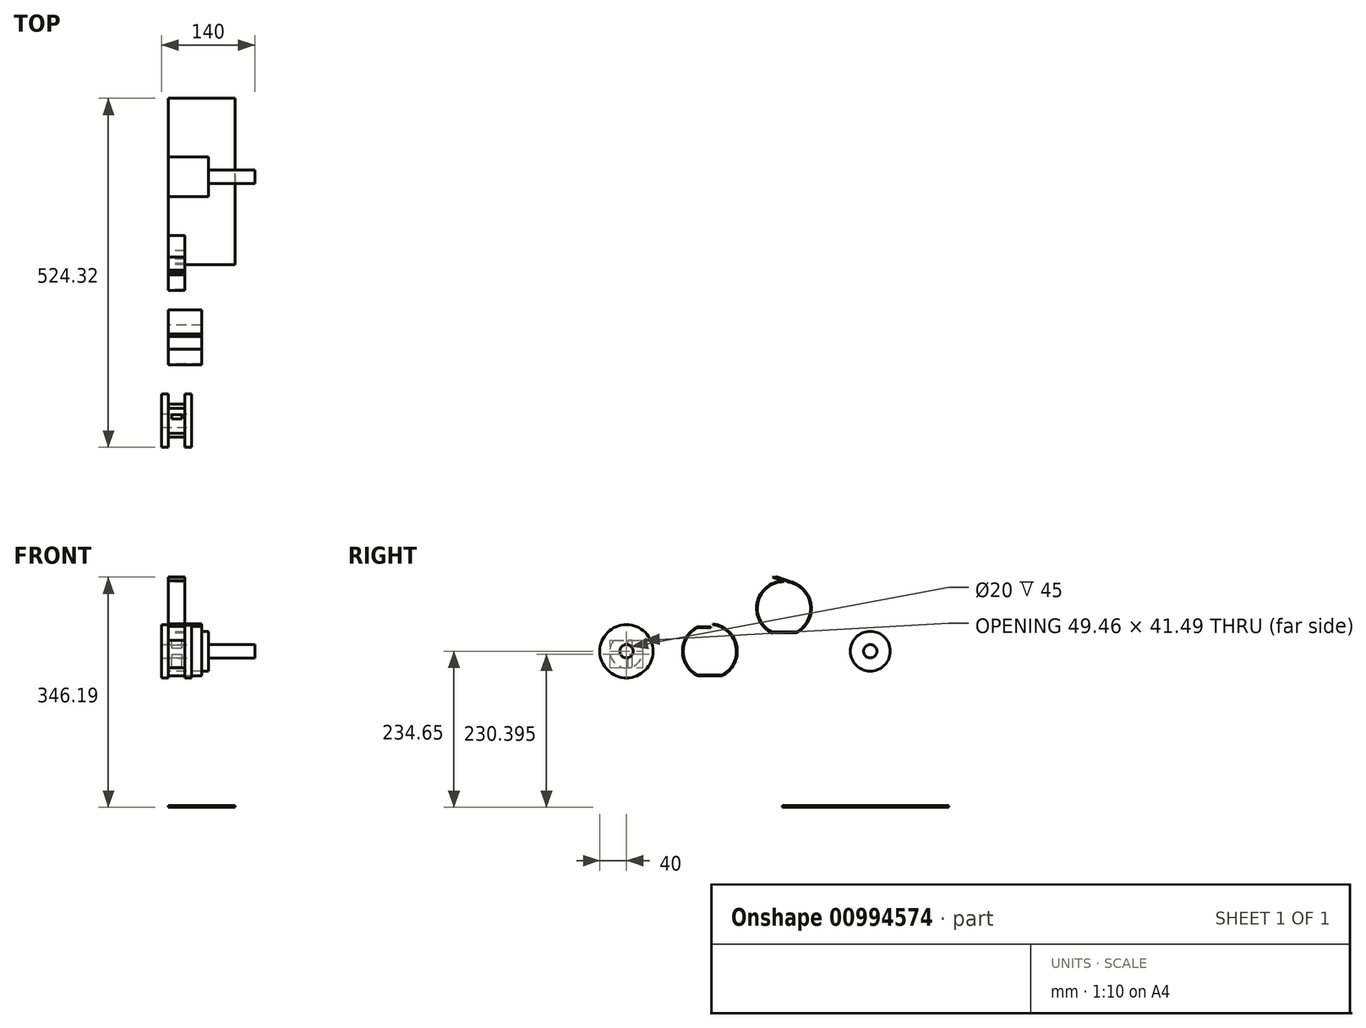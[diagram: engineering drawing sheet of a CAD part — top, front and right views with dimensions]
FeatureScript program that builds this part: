
annotation { "Feature Type Name" : "Feature", "Feature Type Description" : "" }
export const myFeature = defineFeature(function(context is Context, id is Id, definition is map)
    precondition{}
    {
        {
            var Q0;
            Q0=qCreatedBy(makeId("Right.planeOp"),FACE);
            var sketch = newSketch(context, id + "F0", { "sketchPlane" : qUnion([Q0])});
            skArc(sketch, "E0", {"start": v(-18.8, 16.49) * mm, "mid": v(0, -25) * mm, "end": v(18.8, 16.49) * mm});
            skLineSegment(sketch, "E1", {"start": v(-18.8, 16.49) * mm, "end": v(18.8, 16.49) * mm});
            skArc(sketch, "E2", {"start": v(106.71, 35.42) * mm, "mid": v(85.3, 0) * mm, "end": v(106.71, -35.42) * mm});
            skArc(sketch, "E3", {"start": v(107.38, 37.16) * mm, "mid": v(84.05, 0) * mm, "end": v(107.38, -37.16) * mm});
            skLineSegment(sketch, "E4", {"start": v(85.3, 0) * mm, "end": v(165.3, 0) * mm, "construction": true});
            skLineSegment(sketch, "E5", {"start": v(106.71, 35.42) * mm, "end": v(126.7, 35.42) * mm});
            skLineSegment(sketch, "E6", {"start": v(125.3, 37) * mm, "end": v(125.3, 41.25) * mm});
            skLineSegment(sketch, "E7", {"start": v(107.38, 37.16) * mm, "end": v(125.3, 37) * mm});
            skLineSegment(sketch, "E8.MirrorCS", {"start": v(106.71, -35.42) * mm, "end": v(143.9, -35.42) * mm});
            skLineSegment(sketch, "E9.MirrorCS", {"start": v(107.38, -37.16) * mm, "end": v(143.9, -36.82) * mm});
            skPoint(sketch, "E10.end.orphan", {"position": v(104.16, 35.42) * mm});
            skLineSegment(sketch, "E11", {"start": v(126.7, 39.98) * mm, "end": v(126.7, 35.42) * mm});
            skPoint(sketch, "E12.orphan", {"position": v(125.3, 35.42) * mm});
            skArc(sketch, "E13.trimOffspring", {"start": v(143.9, -35.42) * mm, "mid": v(164.3, 8.9) * mm, "end": v(126.7, 39.98) * mm});
            skArc(sketch, "E14.trimOffspring", {"start": v(143.9, -36.82) * mm, "mid": v(165.43, 9.55) * mm, "end": v(125.3, 41.25) * mm});
            skPoint(sketch, "E15.MirrorCS.end.orphan", {"position": v(104.16, -35.42) * mm});
            skPoint(sketch, "E15.MirrorCS.start.orphan", {"position": v(106.71, -35.42) * mm});
            skPoint(sketch, "E16.MirrorCS.end.orphan", {"position": v(146.45, -35.42) * mm});
            skCircle(sketch, "E17", {"center": v(366.34, 0) * mm, "radius": 30 * mm});
            skLineSegment(sketch, "E18", {"start": v(234.32, -232.15) * mm, "end": v(484.32, -232.15) * mm});
            skLineSegment(sketch, "E19", {"start": v(484.32, -232.15) * mm, "end": v(484.32, -234.65) * mm});
            skLineSegment(sketch, "E20", {"start": v(484.32, -234.65) * mm, "end": v(234.32, -234.65) * mm});
            skLineSegment(sketch, "E21", {"start": v(234.32, -234.65) * mm, "end": v(234.32, -232.15) * mm});
            skPoint(sketch, "E22.end.orphan", {"position": v(146.45, 35.42) * mm});
            skPoint(sketch, "E22.start.orphan", {"position": v(143.9, 35.42) * mm});
            skPoint(sketch, "E23.trimOffspring.end.orphan", {"position": v(143.9, 36.82) * mm});
            skLineSegment(sketch, "E24", {"start": v(112.79, 46.1) * mm, "end": v(112.75, 45.15) * mm});
            skArc(sketch, "E25", {"start": v(218.77, 101.6) * mm, "mid": v(195.43, 64.44) * mm, "end": v(218.77, 27.29) * mm});
            skLineSegment(sketch, "E26.MirrorCS", {"start": v(218.1, 29.03) * mm, "end": v(255.28, 29.03) * mm});
            skLineSegment(sketch, "E27.MirrorCS", {"start": v(218.77, 27.29) * mm, "end": v(255.28, 27.62) * mm});
            skPoint(sketch, "E28.end.orphan", {"position": v(215.54, 99.86) * mm});
            skPoint(sketch, "E29.orphan", {"position": v(236.68, 99.86) * mm});
            skArc(sketch, "E30.trimOffspring", {"start": v(255.28, 27.62) * mm, "mid": v(277.64, 69.33) * mm, "end": v(246.1, 104.6) * mm});
            skPoint(sketch, "E31.MirrorCS.end.orphan", {"position": v(215.54, 29.03) * mm});
            skPoint(sketch, "E31.MirrorCS.start.orphan", {"position": v(218.1, 29.03) * mm});
            skPoint(sketch, "E32.MirrorCS.end.orphan", {"position": v(257.83, 29.03) * mm});
            skPoint(sketch, "E33.end.orphan", {"position": v(257.83, 99.86) * mm});
            skPoint(sketch, "E33.start.orphan", {"position": v(255.28, 99.86) * mm});
            skPoint(sketch, "E34.trimOffspring.end.orphan", {"position": v(255.28, 101.27) * mm});
            skArc(sketch, "E35", {"start": v(234.63, 105.64) * mm, "mid": v(196.25, 72.63) * mm, "end": v(218.77, 27.29) * mm});
            skArc(sketch, "E36", {"start": v(255.28, 29.03) * mm, "mid": v(276.11, 71.2) * mm, "end": v(242.43, 104.03) * mm});
            skLineSegment(sketch, "E37", {"start": v(246.1, 104.6) * mm, "end": v(226.45, 111.54) * mm});
            skLineSegment(sketch, "E38", {"start": v(234.63, 105.64) * mm, "end": v(219.42, 111.1) * mm});
            skLineSegment(sketch, "E39", {"start": v(223.76, 111.4) * mm, "end": v(242.43, 104.82) * mm});
            skLineSegment(sketch, "E40", {"start": v(221.42, 111.4) * mm, "end": v(236.45, 106.1) * mm});
            skLineSegment(sketch, "E41", {"start": v(236.45, 106.1) * mm, "end": v(236.45, 104.44) * mm});
            skLineSegment(sketch, "E42", {"start": v(242.43, 104.82) * mm, "end": v(242.43, 104.03) * mm});
            skArc(sketch, "E43.trimOffspring", {"start": v(236.45, 104.44) * mm, "mid": v(197.82, 73.9) * mm, "end": v(218.1, 29.03) * mm});
            skPoint(sketch, "E44.start.orphan", {"position": v(215.71, 112.43) * mm});
            skPoint(sketch, "E45.orphan", {"position": v(223.92, 112.43) * mm});
            skLineSegment(sketch, "E46", {"start": v(223.76, 111.4) * mm, "end": v(226.45, 111.54) * mm});
            skLineSegment(sketch, "E47", {"start": v(221.42, 111.4) * mm, "end": v(219.42, 111.1) * mm});
            skPoint(sketch, "E48.end.orphan", {"position": v(218.22, 111.4) * mm});
            skPoint(sketch, "E49.end.orphan", {"position": v(236.45, 105.73) * mm});
            skSolve(sketch);
        }
        {
            var Q0;
            Q0=makeQuery(id+"F0.imprint","IMPRINT",FACE,{"disambiguationData":[TD([[makeQuery(id+"F0.imprint","IMPRINT",EDGE,{"derivedFrom":sQuery(id+"F0.wireOp",EDGE,"E0")}),1.0]])]});
            extrude(context, id + "F1", {"entities" : qUnion([Q0]), "depth" : 25 * mm, "offsetDistance" : 25 * mm});
        }
        {
            var Q0;
            Q0=makeQuery(id+"F1.opExtrude","CAP_FACE",FACE,{"disambiguationData":[OSD([sQuery(id+"F0.wireOp",EDGE,"E0"),sQuery(id+"F0.wireOp",EDGE,"E1")])],"isStart":false});
            var sketch = newSketch(context, id + "F2", { "sketchPlane" : qUnion([Q0])});
            skCircle(sketch, "E50", {"center": v(0, 0) * mm, "radius": 40 * mm});
            skSolve(sketch);
        }
        {
            var Q0;
            Q0=makeQuery(id+"F2.imprint","IMPRINT",FACE,{"disambiguationData":[TD([[makeQuery(id+"F2.imprint","IMPRINT",EDGE,{"derivedFrom":sQuery(id+"F2.wireOp",EDGE,"E50")}),1.0]])]});
            var Q1;
            Q1=makeQuery(id+"F2.imprint","IMPRINT",FACE,{"disambiguationData":[TD([[makeQuery(id+"F2.imprint","IMPRINT",EDGE,{"derivedFrom":makeQuery(id+"F1.opExtrude","CAP_EDGE",EDGE,{"disambiguationData":[OSD([sQuery(id+"F0.wireOp",EDGE,"E0")])],"isStart":false})}),1.0]])]});
            extrude(context, id + "F3", {"entities" : qUnion([Q0, Q1]), "operationType" : NewBodyOperationType.ADD, "depth" : 10 * mm, "offsetDistance" : 25 * mm});
        }
        {
            var Q0;
            Q0=makeQuery(id+"F1.opExtrude","CAP_FACE",FACE,{"disambiguationData":[OSD([sQuery(id+"F0.wireOp",EDGE,"E0"),sQuery(id+"F0.wireOp",EDGE,"E1")])],"isStart":true});
            var sketch = newSketch(context, id + "F4", { "sketchPlane" : qUnion([Q0])});
            skCircle(sketch, "E51", {"center": v(0, 0) * mm, "radius": 40 * mm});
            skSolve(sketch);
        }
        {
            var Q0;
            Q0=makeQuery(id+"F4.imprint","IMPRINT",FACE,{"disambiguationData":[TD([[makeQuery(id+"F4.imprint","IMPRINT",EDGE,{"derivedFrom":sQuery(id+"F4.wireOp",EDGE,"E51")}),1.0]])]});
            var Q1;
            Q1=makeQuery(id+"F4.imprint","IMPRINT",FACE,{"disambiguationData":[TD([[makeQuery(id+"F4.imprint","IMPRINT",EDGE,{"derivedFrom":makeQuery(id+"F1.opExtrude","CAP_EDGE",EDGE,{"disambiguationData":[OSD([sQuery(id+"F0.wireOp",EDGE,"E0")])],"isStart":true})}),-1.0]])]});
            extrude(context, id + "F5", {"entities" : qUnion([Q0, Q1]), "operationType" : NewBodyOperationType.ADD, "depth" : 10 * mm, "offsetDistance" : 25 * mm});
        }
        {
            var Q0;
            Q0=makeQuery(id+"F1.opExtrude","SWEPT_FACE",FACE,{"disambiguationData":[OSD([sQuery(id+"F0.wireOp",EDGE,"E1")])]});
            var sketch = newSketch(context, id + "F6", { "sketchPlane" : qUnion([Q0])});
            skLineSegment(sketch, "E52.bottom", {"start": v(5, 8.8) * mm, "end": v(20, 8.8) * mm});
            skLineSegment(sketch, "E52.top", {"start": v(5, 2.4) * mm, "end": v(20, 2.4) * mm});
            skLineSegment(sketch, "E52.left", {"start": v(5, 8.8) * mm, "end": v(5, 2.4) * mm});
            skLineSegment(sketch, "E52.right", {"start": v(20, 8.8) * mm, "end": v(20, 2.4) * mm});
            skSolve(sketch);
        }
        {
            var Q0;
            Q0=makeQuery(id+"F6.imprint","IMPRINT",FACE,{"disambiguationData":[TD([[makeQuery(id+"F6.imprint","IMPRINT",EDGE,{"derivedFrom":sQuery(id+"F6.wireOp",EDGE,"E52.bottom")}),-1.0]])]});
            extrude(context, id + "F7", {"entities" : qUnion([Q0]), "operationType" : NewBodyOperationType.REMOVE, "endBound" : BoundingType.UP_TO_NEXT, "oppositeDirection" : true, "depth" : 5 * mm, "offsetDistance" : 25 * mm});
        }
        {
            var Q0;
            Q0=makeQuery(id+"F0.imprint","IMPRINT",FACE,{"disambiguationData":[TD([[makeQuery(id+"F0.imprint","IMPRINT",EDGE,{"derivedFrom":sQuery(id+"F0.wireOp",EDGE,"E2")}),-1.0]])]});
            extrude(context, id + "F8", {"entities" : qUnion([Q0]), "depth" : 50 * mm, "offsetDistance" : 25 * mm});
        }
        {
            var Q0;
            Q0=makeQuery(id+"F3.opExtrude","CAP_FACE",FACE,{"disambiguationData":[OSD([sQuery(id+"F2.wireOp",EDGE,"E50")])],"isStart":false});
            var sketch = newSketch(context, id + "F9", { "sketchPlane" : qUnion([Q0])});
            skCircle(sketch, "E53", {"center": v(0, 0) * mm, "radius": 10 * mm});
            skSolve(sketch);
        }
        {
            var Q0;
            Q0=makeQuery(id+"F9.imprint","IMPRINT",FACE,{"disambiguationData":[TD([[makeQuery(id+"F9.imprint","IMPRINT",EDGE,{"derivedFrom":sQuery(id+"F9.wireOp",EDGE,"E53")}),1.0]])]});
            extrude(context, id + "F10", {"entities" : qUnion([Q0]), "operationType" : NewBodyOperationType.REMOVE, "endBound" : BoundingType.UP_TO_NEXT, "oppositeDirection" : true, "depth" : 25 * mm, "offsetDistance" : 25 * mm});
        }
        {
            var Q0;
            Q0=makeQuery(id+"F0.imprint","IMPRINT",FACE,{"disambiguationData":[TD([[makeQuery(id+"F0.imprint","IMPRINT",EDGE,{"derivedFrom":sQuery(id+"F0.wireOp",EDGE,"E17")}),1.0]])]});
            extrude(context, id + "F11", {"entities" : qUnion([Q0]), "depth" : 60 * mm, "offsetDistance" : 25 * mm});
        }
        {
            var Q0;
            Q0=makeQuery(id+"F11.opExtrude","CAP_FACE",FACE,{"disambiguationData":[OSD([sQuery(id+"F0.wireOp",EDGE,"E17")])],"isStart":false});
            var sketch = newSketch(context, id + "F12", { "sketchPlane" : qUnion([Q0])});
            skCircle(sketch, "E54", {"center": v(366.34, 0) * mm, "radius": 10 * mm});
            skSolve(sketch);
        }
        {
            var Q0;
            Q0=makeQuery(id+"F12.imprint","IMPRINT",FACE,{"disambiguationData":[TD([[makeQuery(id+"F12.imprint","IMPRINT",EDGE,{"derivedFrom":sQuery(id+"F12.wireOp",EDGE,"E54")}),1.0]])]});
            extrude(context, id + "F13", {"entities" : qUnion([Q0]), "operationType" : NewBodyOperationType.ADD, "depth" : 70 * mm, "offsetDistance" : 25 * mm});
        }
        {
            var Q0;
            Q0=makeQuery(id+"F0.imprint","IMPRINT",FACE,{"disambiguationData":[TD([[makeQuery(id+"F0.imprint","IMPRINT",EDGE,{"derivedFrom":sQuery(id+"F0.wireOp",EDGE,"E18")}),-1.0]])]});
            extrude(context, id + "F14", {"entities" : qUnion([Q0]), "depth" : 100 * mm, "offsetDistance" : 25 * mm});
        }
        {
            var Q0;
            Q0=makeQuery(id+"F8.opExtrude","SWEPT_FACE",FACE,{"disambiguationData":[OSD([sQuery(id+"F0.wireOp",EDGE,"E6")])]});
            extrude(context, id + "F15", {"entities" : qUnion([Q0]), "operationType" : NewBodyOperationType.REMOVE, "oppositeDirection" : true, "depth" : 5 * mm, "offsetDistance" : 25 * mm});
        }
        {
            var Q0;
            Q0=makeQuery(id+"F0.imprint","IMPRINT",FACE,{"disambiguationData":[TD([[makeQuery(id+"F0.imprint","IMPRINT",EDGE,{"derivedFrom":sQuery(id+"F0.wireOp",EDGE,"E26.MirrorCS")}),-1.0]])]});
            extrude(context, id + "F16", {"entities" : qUnion([Q0]), "depth" : 25 * mm, "offsetDistance" : 25 * mm});
        }
    });
